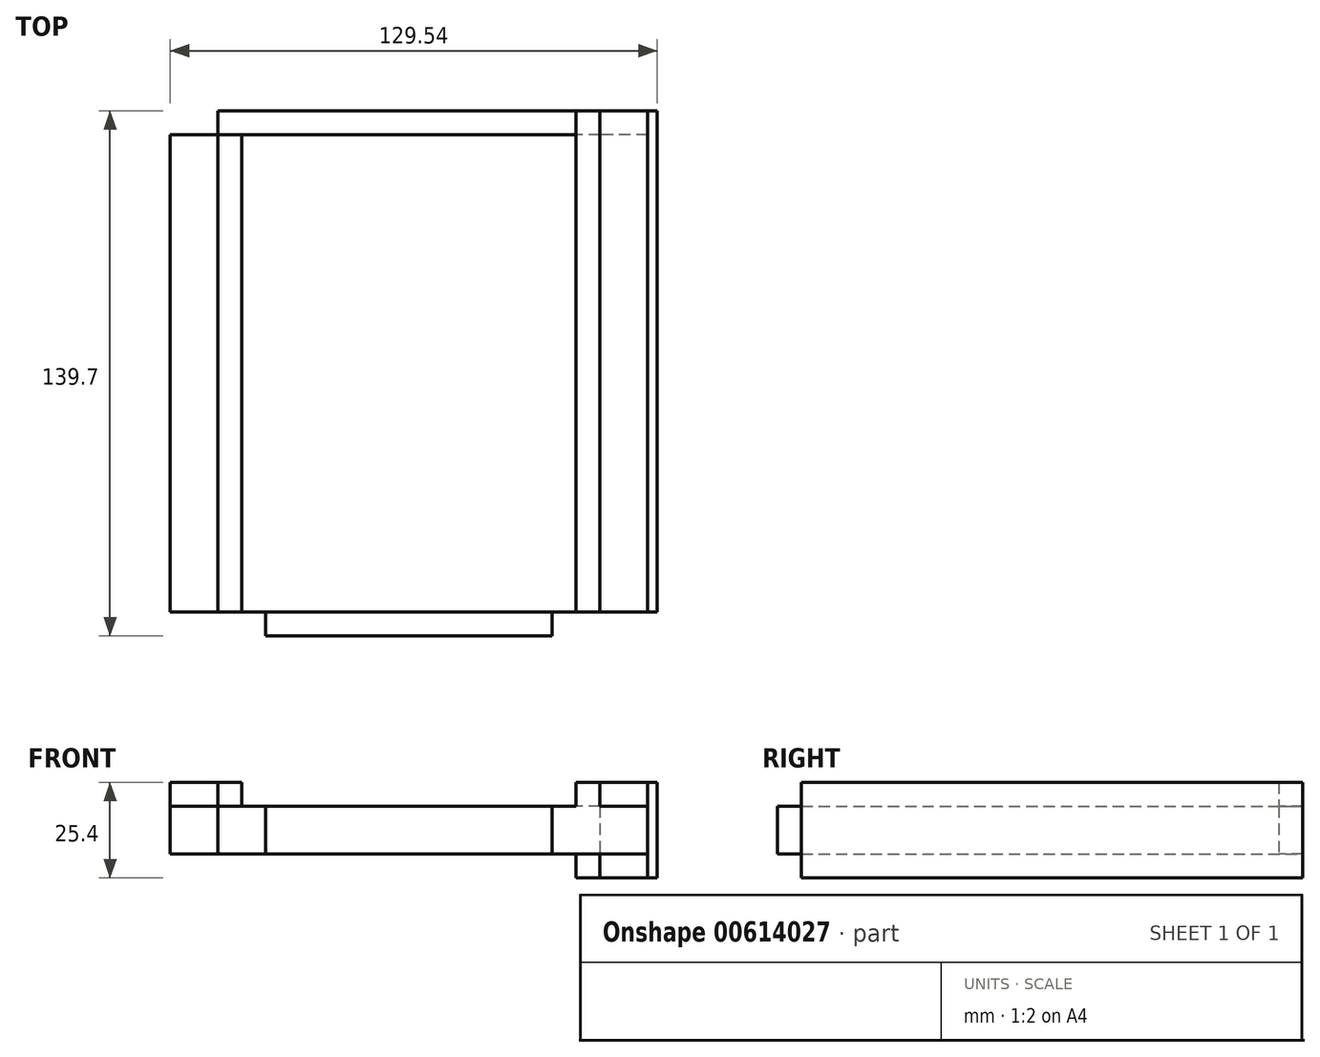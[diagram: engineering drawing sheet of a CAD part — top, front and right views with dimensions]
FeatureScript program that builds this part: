
annotation { "Feature Type Name" : "Feature", "Feature Type Description" : "" }
export const myFeature = defineFeature(function(context is Context, id is Id, definition is map)
    precondition{}
    {
        {
            var Q0;
            Q0=qCreatedBy(makeId("Top.planeOp"),FACE);
            var sketch = newSketch(context, id + "F0", { "sketchPlane" : qUnion([Q0])});
            skLineSegment(sketch, "E0.bottom", {"start": v(45, 0) * mm, "end": v(-56.6, 0) * mm});
            skLineSegment(sketch, "E0.top", {"start": v(45, 127) * mm, "end": v(-56.6, 127) * mm});
            skLineSegment(sketch, "E0.left", {"start": v(45, 0) * mm, "end": v(45, 127) * mm});
            skLineSegment(sketch, "E0.right", {"start": v(-56.6, 0) * mm, "end": v(-56.6, 127) * mm});
            skSolve(sketch);
        }
        {
            var Q0;
            Q0 = qSketchRegion(id + "F0", true);
            extrude(context, id + "F1", {"entities" : qUnion([Q0]), "depth" : 12.7 * mm, "offsetDistance" : 25.4 * mm});
        }
        {
            var Q0;
            Q0=makeQuery(id+"F1.opExtrude","SWEPT_FACE",FACE,{"disambiguationData":[OSD([sQuery(id+"F0.wireOp",EDGE,"E0.bottom")])]});
            var sketch = newSketch(context, id + "F2", { "sketchPlane" : qUnion([Q0])});
            skLineSegment(sketch, "E1", {"start": v(-43.9, 0) * mm, "end": v(32.3, 0) * mm});
            skLineSegment(sketch, "E2", {"start": v(-43.9, 0) * mm, "end": v(-43.9, 12.7) * mm});
            skLineSegment(sketch, "E3", {"start": v(-43.9, 12.7) * mm, "end": v(32.3, 12.7) * mm});
            skLineSegment(sketch, "E4", {"start": v(32.3, 12.7) * mm, "end": v(32.3, 0) * mm});
            skSolve(sketch);
        }
        {
            var Q0;
            Q0 = qSketchRegion(id + "F2", true);
            extrude(context, id + "F3", {"entities" : qUnion([Q0]), "depth" : 6.35 * mm, "offsetDistance" : 25.4 * mm});
        }
        {
            var Q0;
            Q0=makeQuery(id+"F1.opExtrude","SWEPT_FACE",FACE,{"disambiguationData":[OSD([sQuery(id+"F0.wireOp",EDGE,"E0.left")])]});
            var sketch = newSketch(context, id + "F4", { "sketchPlane" : qUnion([Q0])});
            skLineSegment(sketch, "E5.bottom", {"start": v(0, 12.7) * mm, "end": v(127, 12.7) * mm});
            skLineSegment(sketch, "E5.top", {"start": v(0, 0) * mm, "end": v(127, 0) * mm});
            skLineSegment(sketch, "E5.left", {"start": v(0, 12.7) * mm, "end": v(0, 0) * mm});
            skLineSegment(sketch, "E5.right", {"start": v(127, 12.7) * mm, "end": v(127, 0) * mm});
            skSolve(sketch);
        }
        {
            var Q0;
            Q0=makeQuery(id+"F4.imprint","IMPRINT",FACE,{"disambiguationData":[TD([[makeQuery(id+"F4.imprint","IMPRINT",EDGE,{"derivedFrom":sQuery(id+"F4.wireOp",EDGE,"E5.bottom")}),-1.0]])]});
            var sketch = newSketch(context, id + "F5", { "sketchPlane" : qUnion([Q0])});
            skLineSegment(sketch, "E6", {"start": v(0, 0) * mm, "end": v(0, -6.35) * mm});
            skLineSegment(sketch, "E7", {"start": v(0, 0) * mm, "end": v(0, 19.05) * mm});
            skLineSegment(sketch, "E8", {"start": v(0, 19.05) * mm, "end": v(133.35, 19.05) * mm});
            skLineSegment(sketch, "E9", {"start": v(133.35, 19.05) * mm, "end": v(133.35, 12.7) * mm});
            skLineSegment(sketch, "E10", {"start": v(133.35, 12.7) * mm, "end": v(0, 12.7) * mm});
            skLineSegment(sketch, "E11", {"start": v(0, -6.35) * mm, "end": v(133.35, -6.35) * mm});
            skLineSegment(sketch, "E12", {"start": v(133.35, -6.35) * mm, "end": v(133.35, 0) * mm});
            skLineSegment(sketch, "E13", {"start": v(133.35, 0) * mm, "end": v(0, 0) * mm});
            skLineSegment(sketch, "E14", {"start": v(133.35, 12.7) * mm, "end": v(133.35, 0) * mm});
            skSolve(sketch);
        }
        {
            var Q0;
            {var subQ5=sQuery(id+"F5.wireOp",EDGE,"E8");Q0=makeQuery(id+"F5.imprint","IMPRINT",FACE,{"disambiguationData":[TD([[makeQuery(id+"F5.imprint","IMPRINT",EDGE,{"derivedFrom":subQ5}),-1.0]])]});}
            extrude(context, id + "F6", {"entities" : qUnion([Q0]), "oppositeDirection" : true, "depth" : 6.35 * mm, "offsetDistance" : 25.4 * mm});
        }
        {
            var Q0;
            Q0=makeQuery(id+"F4.imprint","IMPRINT",FACE,{"disambiguationData":[TD([[makeQuery(id+"F4.imprint","IMPRINT",EDGE,{"derivedFrom":sQuery(id+"F4.wireOp",EDGE,"E5.bottom")}),-1.0]])]});
            extrude(context, id + "F7", {"entities" : qUnion([Q0]), "operationType" : NewBodyOperationType.ADD, "depth" : 12.7 * mm, "offsetDistance" : 25.4 * mm});
        }
        {
            var Q0;
            {var subQ1=sQuery(id+"F5.wireOp",EDGE,"E6");Q0=makeQuery(id+"F5.imprint","IMPRINT",FACE,{"disambiguationData":[TD([[makeQuery(id+"F5.imprint","IMPRINT",EDGE,{"derivedFrom":subQ1}),1.0]])]});}
            extrude(context, id + "F8", {"entities" : qUnion([Q0]), "oppositeDirection" : true, "depth" : 6.35 * mm, "offsetDistance" : 25.4 * mm});
        }
        {
            var Q0;
            {var subQ1=sQuery(id+"F5.wireOp",EDGE,"E6");Q0=makeQuery(id+"F5.imprint","IMPRINT",FACE,{"disambiguationData":[TD([[makeQuery(id+"F5.imprint","IMPRINT",EDGE,{"derivedFrom":subQ1}),1.0]])]});}
            var Q1;
            {var subQ5=sQuery(id+"F5.wireOp",EDGE,"E8");Q1=makeQuery(id+"F5.imprint","IMPRINT",FACE,{"disambiguationData":[TD([[makeQuery(id+"F5.imprint","IMPRINT",EDGE,{"derivedFrom":subQ5}),-1.0]])]});}
            extrude(context, id + "F9", {"entities" : qUnion([Q0, Q1]), "depth" : 12.7 * mm, "offsetDistance" : 25.4 * mm});
        }
        {
            var Q0;
            Q0=makeQuery(id+"F7.opExtrude","CAP_FACE",FACE,{"disambiguationData":[OSD([sQuery(id+"F4.wireOp",EDGE,"E5.bottom"),sQuery(id+"F4.wireOp",EDGE,"E5.top"),sQuery(id+"F4.wireOp",EDGE,"E5.left"),sQuery(id+"F4.wireOp",EDGE,"E5.right")])],"isStart":false});
            var sketch = newSketch(context, id + "F10", { "sketchPlane" : qUnion([Q0])});
            skLineSegment(sketch, "E15.bottom", {"start": v(0, -6.35) * mm, "end": v(133.35, -6.35) * mm});
            skLineSegment(sketch, "E15.top", {"start": v(0, 19.05) * mm, "end": v(133.35, 19.05) * mm});
            skLineSegment(sketch, "E15.left", {"start": v(0, -6.35) * mm, "end": v(0, 19.05) * mm});
            skLineSegment(sketch, "E15.right", {"start": v(133.35, -6.35) * mm, "end": v(133.35, 19.05) * mm});
            skSolve(sketch);
        }
        {
            var Q0;
            Q0 = qSketchRegion(id + "F10", true);
            extrude(context, id + "F11", {"entities" : qUnion([Q0]), "depth" : 2.54 * mm, "offsetDistance" : 25.4 * mm});
        }
        {
            var Q0;
            Q0=makeQuery(id+"F7.boolean.opBoolean","MERGE",FACE,{"derivedFrom":[makeQuery(id+"F1.opExtrude","SWEPT_FACE",FACE,{"disambiguationData":[OSD([sQuery(id+"F0.wireOp",EDGE,"E0.top")])]}),makeQuery(id+"F7.opExtrude","SWEPT_FACE",FACE,{"disambiguationData":[OSD([sQuery(id+"F4.wireOp",EDGE,"E5.right")])]})]});
            var sketch = newSketch(context, id + "F12", { "sketchPlane" : qUnion([Q0])});
            skLineSegment(sketch, "E16", {"start": v(-57.7, 0) * mm, "end": v(-57.7, 12.7) * mm});
            skLineSegment(sketch, "E17", {"start": v(-57.7, 12.7) * mm, "end": v(-45, 12.7) * mm});
            skLineSegment(sketch, "E18", {"start": v(-45, 12.7) * mm, "end": v(-45, 0) * mm});
            skLineSegment(sketch, "E19", {"start": v(-45, 0) * mm, "end": v(-57.7, 0) * mm});
            skSolve(sketch);
        }
        {
            var Q0;
            Q0 = qSketchRegion(id + "F12", true);
            extrude(context, id + "F13", {"entities" : qUnion([Q0]), "depth" : 6.35 * mm, "offsetDistance" : 25.4 * mm});
        }
        {
            var Q0;
            Q0=makeQuery(id+"F1.opExtrude","SWEPT_FACE",FACE,{"disambiguationData":[OSD([sQuery(id+"F0.wireOp",EDGE,"E0.right")])]});
            var sketch = newSketch(context, id + "F14", { "sketchPlane" : qUnion([Q0])});
            skLineSegment(sketch, "E20.bottom", {"start": v(-127, 0) * mm, "end": v(-133.35, 0) * mm});
            skLineSegment(sketch, "E20.top", {"start": v(-127, 12.7) * mm, "end": v(-133.35, 12.7) * mm});
            skLineSegment(sketch, "E20.left", {"start": v(-127, 0) * mm, "end": v(-127, 12.7) * mm});
            skLineSegment(sketch, "E20.right", {"start": v(-133.35, 0) * mm, "end": v(-133.35, 12.7) * mm});
            skSolve(sketch);
        }
        {
            var Q0;
            Q0=makeQuery(id+"F14.imprint","IMPRINT",FACE,{"disambiguationData":[TD([[makeQuery(id+"F14.imprint","IMPRINT",EDGE,{"derivedFrom":sQuery(id+"F14.wireOp",EDGE,"E20.bottom")}),-1.0]])]});
            extrude(context, id + "F15", {"entities" : qUnion([Q0]), "oppositeDirection" : true, "depth" : 101.6 * mm, "offsetDistance" : 25.4 * mm});
        }
        {
            var Q0;
            Q0=makeQuery(id+"F1.opExtrude","SWEPT_FACE",FACE,{"disambiguationData":[OSD([sQuery(id+"F0.wireOp",EDGE,"E0.right")])]});
            var sketch = newSketch(context, id + "F16", { "sketchPlane" : qUnion([Q0])});
            skLineSegment(sketch, "E21.bottom", {"start": v(-127, 12.7) * mm, "end": v(0, 12.7) * mm});
            skLineSegment(sketch, "E21.top", {"start": v(-127, 0) * mm, "end": v(0, 0) * mm});
            skLineSegment(sketch, "E21.left", {"start": v(-127, 12.7) * mm, "end": v(-127, 0) * mm});
            skLineSegment(sketch, "E21.right", {"start": v(0, 12.7) * mm, "end": v(0, 0) * mm});
            skSolve(sketch);
        }
        {
            var Q0;
            Q0 = qSketchRegion(id + "F16", true);
            extrude(context, id + "F17", {"entities" : qUnion([Q0]), "depth" : 12.7 * mm, "offsetDistance" : 25.4 * mm});
        }
        {
            var Q0;
            Q0=makeQuery(id+"F17.opExtrude","SWEPT_FACE",FACE,{"disambiguationData":[OSD([sQuery(id+"F16.wireOp",EDGE,"E21.bottom")])]});
            var sketch = newSketch(context, id + "F18", { "sketchPlane" : qUnion([Q0])});
            skLineSegment(sketch, "E22.bottom", {"start": v(-56.6, 127) * mm, "end": v(-69.3, 127) * mm});
            skLineSegment(sketch, "E22.top", {"start": v(-56.6, 0) * mm, "end": v(-69.3, 0) * mm});
            skLineSegment(sketch, "E22.left", {"start": v(-56.6, 127) * mm, "end": v(-56.6, 0) * mm});
            skLineSegment(sketch, "E22.right", {"start": v(-69.3, 127) * mm, "end": v(-69.3, 0) * mm});
            skSolve(sketch);
        }
        {
            var Q0;
            Q0 = qSketchRegion(id + "F18", true);
            extrude(context, id + "F19", {"entities" : qUnion([Q0]), "depth" : 6.35 * mm, "offsetDistance" : 25.4 * mm});
        }
        {
            var Q0;
            Q0=makeQuery(id+"F19.opExtrude","SWEPT_FACE",FACE,{"disambiguationData":[OSD([sQuery(id+"F18.wireOp",EDGE,"E22.left")])]});
            var sketch = newSketch(context, id + "F20", { "sketchPlane" : qUnion([Q0])});
            skLineSegment(sketch, "E23.bottom", {"start": v(0, 19.05) * mm, "end": v(127, 19.05) * mm});
            skLineSegment(sketch, "E23.top", {"start": v(0, 12.7) * mm, "end": v(127, 12.7) * mm});
            skLineSegment(sketch, "E23.left", {"start": v(0, 19.05) * mm, "end": v(0, 12.7) * mm});
            skLineSegment(sketch, "E23.right", {"start": v(127, 19.05) * mm, "end": v(127, 12.7) * mm});
            skSolve(sketch);
        }
        {
            var Q0;
            Q0=makeQuery(id+"F20.imprint","IMPRINT",FACE,{"disambiguationData":[TD([[makeQuery(id+"F20.imprint","IMPRINT",EDGE,{"derivedFrom":sQuery(id+"F20.wireOp",EDGE,"E23.bottom")}),-1.0]])]});
            extrude(context, id + "F21", {"entities" : qUnion([Q0]), "depth" : 6.35 * mm, "offsetDistance" : 25.4 * mm});
        }
    });
